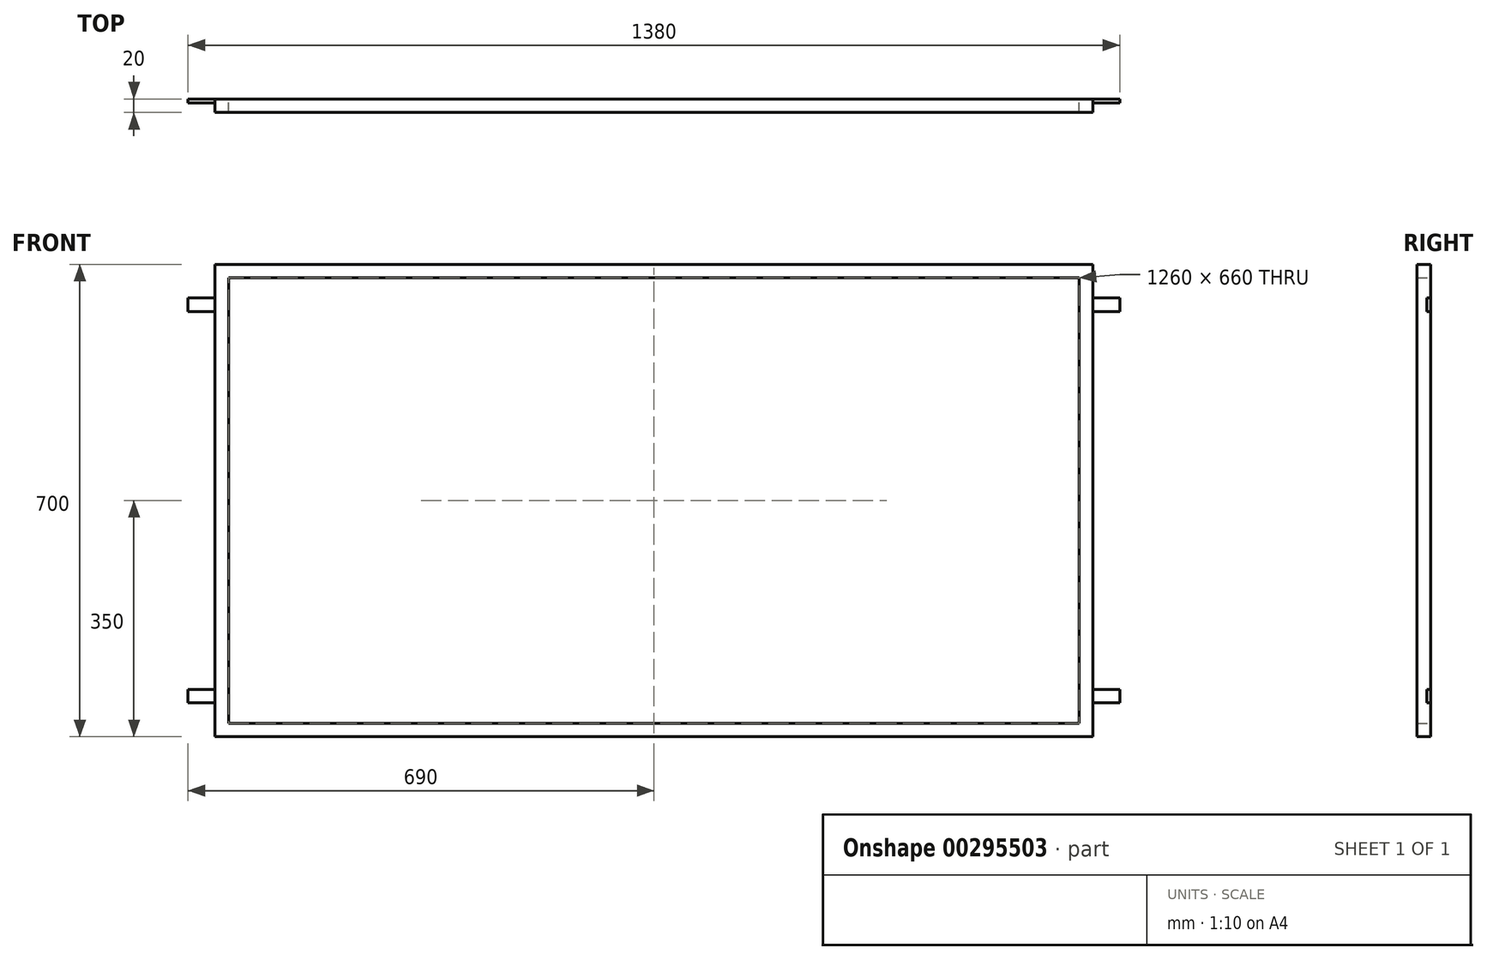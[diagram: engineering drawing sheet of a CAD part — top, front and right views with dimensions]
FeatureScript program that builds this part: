
annotation { "Feature Type Name" : "Feature", "Feature Type Description" : "" }
export const myFeature = defineFeature(function(context is Context, id is Id, definition is map)
    precondition{}
    {
        {
            var Q0;
            Q0=qCreatedBy(makeId("Front.planeOp"),FACE);
            var sketch = newSketch(context, id + "F0", { "sketchPlane" : qUnion([Q0])});
            skLineSegment(sketch, "E0.bottom", {"start": v(650, 350) * mm, "end": v(-650, 350) * mm});
            skLineSegment(sketch, "E0.top", {"start": v(650, -350) * mm, "end": v(-650, -350) * mm});
            skLineSegment(sketch, "E0.left", {"start": v(650, 350) * mm, "end": v(650, -350) * mm});
            skLineSegment(sketch, "E0.right", {"start": v(-650, 350) * mm, "end": v(-650, -350) * mm});
            skPoint(sketch, "E0.middle", {"position": v(0, 0) * mm});
            skLineSegment(sketch, "E1.0", {"start": v(-630, 330) * mm, "end": v(-630, -330) * mm});
            skLineSegment(sketch, "E1.1", {"start": v(630, 330) * mm, "end": v(-630, 330) * mm});
            skLineSegment(sketch, "E1.2", {"start": v(630, 330) * mm, "end": v(630, -330) * mm});
            skLineSegment(sketch, "E1.3", {"start": v(630, -330) * mm, "end": v(-630, -330) * mm});
            skSolve(sketch);
        }
        {
            var Q0;
            Q0 = qSketchRegion(id + "F0", true);
            var Q1;
            Q1=makeQuery(id+"F0.imprint","IMPRINT",FACE,{"disambiguationData":[TD([[makeQuery(id+"F0.imprint","IMPRINT",EDGE,{"derivedFrom":sQuery(id+"F0.wireOp",EDGE,"E0.bottom")}),1.0]])]});
            extrude(context, id + "F1", {"entities" : qUnion([Q0, Q1]), "depth" : 20 * mm});
        }
        {
            var Q0;
            Q0=qCreatedBy(makeId("Front.planeOp"),FACE);
            var sketch = newSketch(context, id + "F2", { "sketchPlane" : qUnion([Q0])});
            skLineSegment(sketch, "E2.bottom", {"start": v(650, -300) * mm, "end": v(690, -300) * mm});
            skLineSegment(sketch, "E2.top", {"start": v(650, -280) * mm, "end": v(690, -280) * mm});
            skLineSegment(sketch, "E2.left", {"start": v(650, -300) * mm, "end": v(650, -280) * mm});
            skLineSegment(sketch, "E2.right", {"start": v(690, -300) * mm, "end": v(690, -280) * mm});
            skSolve(sketch);
        }
        {
            var Q0;
            Q0=makeQuery(id+"F2.imprint","IMPRINT",FACE,{"disambiguationData":[TD([[makeQuery(id+"F2.imprint","IMPRINT",EDGE,{"derivedFrom":sQuery(id+"F2.wireOp",EDGE,"E2.bottom")}),1.0]])]});
            extrude(context, id + "F3", {"entities" : qUnion([Q0]), "operationType" : NewBodyOperationType.ADD, "depth" : 6 * mm});
        }
        {
            var Q0;
            Q0=makeQuery(id+"F1.opExtrude","SWEPT_BODY",BODY,{"disambiguationData":[OSD([sQuery(id+"F0.wireOp",EDGE,"E0.bottom"),sQuery(id+"F0.wireOp",EDGE,"E0.top"),sQuery(id+"F0.wireOp",EDGE,"E0.left"),sQuery(id+"F0.wireOp",EDGE,"E0.right"),sQuery(id+"F0.wireOp",EDGE,"E1.0"),sQuery(id+"F0.wireOp",EDGE,"E1.1"),sQuery(id+"F0.wireOp",EDGE,"E1.2"),sQuery(id+"F0.wireOp",EDGE,"E1.3")])]});
            var Q1;
            Q1=qCreatedBy(makeId("Top.planeOp"),FACE);
            mirror(context, id + "F4", {"operationType" : NewBodyOperationType.ADD, "entities" : qUnion([Q0]), "mirrorPlane" : qUnion([Q1])});
        }
        {
            var Q0;
            Q0=makeQuery(id+"F1.opExtrude","SWEPT_BODY",BODY,{"disambiguationData":[OSD([sQuery(id+"F0.wireOp",EDGE,"E0.bottom"),sQuery(id+"F0.wireOp",EDGE,"E0.top"),sQuery(id+"F0.wireOp",EDGE,"E0.left"),sQuery(id+"F0.wireOp",EDGE,"E0.right"),sQuery(id+"F0.wireOp",EDGE,"E1.0"),sQuery(id+"F0.wireOp",EDGE,"E1.1"),sQuery(id+"F0.wireOp",EDGE,"E1.2"),sQuery(id+"F0.wireOp",EDGE,"E1.3")])]});
            var Q1;
            Q1=qCreatedBy(makeId("Right.planeOp"),FACE);
            mirror(context, id + "F5", {"operationType" : NewBodyOperationType.ADD, "entities" : qUnion([Q0]), "mirrorPlane" : qUnion([Q1])});
        }
    });
